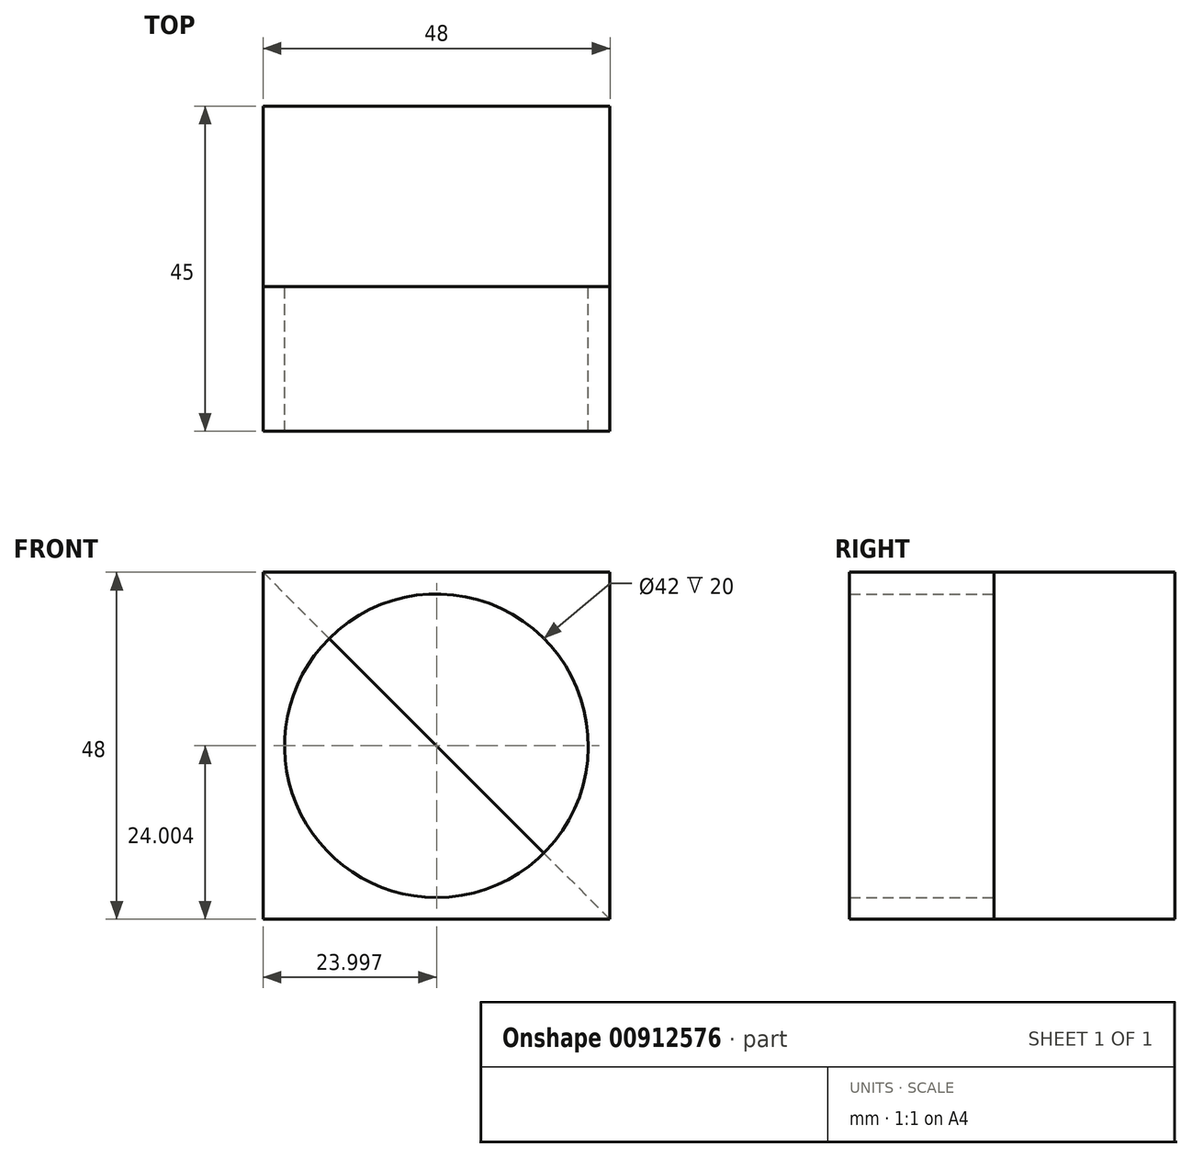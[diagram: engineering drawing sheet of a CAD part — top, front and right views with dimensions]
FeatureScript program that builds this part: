
annotation { "Feature Type Name" : "Feature", "Feature Type Description" : "" }
export const myFeature = defineFeature(function(context is Context, id is Id, definition is map)
    precondition{}
    {
        {
            var Q0;
            Q0=qCreatedBy(makeId("Front.planeOp"),FACE);
            var sketch = newSketch(context, id + "F0", { "sketchPlane" : qUnion([Q0])});
            skLineSegment(sketch, "E0.bottom", {"start": v(-37.2, 26.25) * mm, "end": v(10.8, 26.25) * mm});
            skLineSegment(sketch, "E0.top", {"start": v(-37.2, -21.75) * mm, "end": v(10.8, -21.75) * mm});
            skLineSegment(sketch, "E0.left", {"start": v(-37.2, 26.25) * mm, "end": v(-37.2, -21.75) * mm});
            skLineSegment(sketch, "E0.right", {"start": v(10.8, 26.25) * mm, "end": v(10.8, -21.75) * mm});
            skLineSegment(sketch, "E1", {"start": v(-37.2, 26.25) * mm, "end": v(10.8, -21.75) * mm});
            skLineSegment(sketch, "E2", {"start": v(10.8, 26.25) * mm, "end": v(-37.2, -21.75) * mm});
            skSolve(sketch);
        }
        {
            var Q0;
            {var subQ0=sQuery(id+"F0.wireOp",EDGE,"E0.left");Q0=makeQuery(id+"F0.imprint","IMPRINT",FACE,{"disambiguationData":[TD([[makeQuery(id+"F0.imprint","IMPRINT",EDGE,{"derivedFrom":subQ0}),1.0]])]});}
            var Q1;
            {var subQ0=sQuery(id+"F0.wireOp",EDGE,"E0.bottom");Q1=makeQuery(id+"F0.imprint","IMPRINT",FACE,{"disambiguationData":[TD([[makeQuery(id+"F0.imprint","IMPRINT",EDGE,{"derivedFrom":subQ0}),-1.0]])]});}
            var Q2;
            {var subQ0=sQuery(id+"F0.wireOp",EDGE,"E0.right");Q2=makeQuery(id+"F0.imprint","IMPRINT",FACE,{"disambiguationData":[TD([[makeQuery(id+"F0.imprint","IMPRINT",EDGE,{"derivedFrom":subQ0}),-1.0]])]});}
            var Q3;
            {var subQ0=sQuery(id+"F0.wireOp",EDGE,"E0.top");Q3=makeQuery(id+"F0.imprint","IMPRINT",FACE,{"disambiguationData":[TD([[makeQuery(id+"F0.imprint","IMPRINT",EDGE,{"derivedFrom":subQ0}),1.0]])]});}
            extrude(context, id + "F1", {"entities" : qUnion([Q0, Q1, Q2, Q3]), "depth" : 20 * mm, "offsetDistance" : 25 * mm});
        }
        {
            var Q0;
            Q0=makeQuery(id+"F1.opExtrude","CAP_FACE",FACE,{"disambiguationData":[OSD([sQuery(id+"F0.wireOp",EDGE,"E0.bottom"),sQuery(id+"F0.wireOp",EDGE,"E0.top"),sQuery(id+"F0.wireOp",EDGE,"E0.left"),sQuery(id+"F0.wireOp",EDGE,"E0.right")])],"isStart":true});
            var sketch = newSketch(context, id + "F2", { "sketchPlane" : qUnion([Q0])});
            skLineSegment(sketch, "E3", {"start": v(37.2, -21.75) * mm, "end": v(-10.8, 26.25) * mm});
            skLineSegment(sketch, "E4", {"start": v(-10.8, 26.25) * mm, "end": v(-10.8, -21.75) * mm});
            skLineSegment(sketch, "E5", {"start": v(-10.8, -21.75) * mm, "end": v(37.2, 26.25) * mm});
            skLineSegment(sketch, "E6", {"start": v(37.2, 26.25) * mm, "end": v(13.2, 2.25) * mm});
            skLineSegment(sketch, "E7", {"start": v(13.2, 2.25) * mm, "end": v(13.2, 26.25) * mm});
            skLineSegment(sketch, "E8", {"start": v(13.2, 26.25) * mm, "end": v(13.2, 2.25) * mm});
            skSolve(sketch);
        }
        {
            var Q0;
            Q0=sQuery(id+"F2.wireOp",VERTEX,"E6.end");
            var Q1;
            Q1=makeQuery(id+"F1.opExtrude","SWEPT_BODY",BODY,{"disambiguationData":[OSD([sQuery(id+"F0.wireOp",EDGE,"E0.bottom"),sQuery(id+"F0.wireOp",EDGE,"E0.top"),sQuery(id+"F0.wireOp",EDGE,"E0.left"),sQuery(id+"F0.wireOp",EDGE,"E0.right")])]});
            hole(context, id + "F3", {"style" : HoleStyle.SIMPLE, "endStyle" : HoleEndStyle.BLIND, "holeDiameter" : 42 * mm, "majorDiameter" : 5 * mm, "holeDepth" : 50 * mm, "isTappedThrough" : true, "tappedDepth" : 12 * mm, "tapClearance" : 3, "locations" : qUnion([Q0]), "scope" : qUnion([Q1])});
        }
        {
            var Q0;
            {var subQ2=sQuery(id+"F2.wireOp",EDGE,"E5");Q0=makeQuery(id+"F2.imprint","IMPRINT",FACE,{"disambiguationData":[TD([[makeQuery(id+"F2.imprint","IMPRINT",EDGE,{"derivedFrom":subQ2}),-1.0]])]});}
            var Q1;
            {var subQ0=sQuery(id+"F2.wireOp",EDGE,"E6");Q1=makeQuery(id+"F2.imprint","IMPRINT",FACE,{"disambiguationData":[TD([[makeQuery(id+"F2.imprint","IMPRINT",EDGE,{"derivedFrom":subQ0}),-1.0]])]});}
            var Q2;
            {var subQ2=sQuery(id+"F2.wireOp",EDGE,"E6");Q2=makeQuery(id+"F2.imprint","IMPRINT",FACE,{"disambiguationData":[TD([[makeQuery(id+"F2.imprint","IMPRINT",EDGE,{"derivedFrom":subQ2}),1.0]])]});}
            extrude(context, id + "F4", {"entities" : qUnion([Q0, Q1, Q2]), "operationType" : NewBodyOperationType.ADD, "depth" : 25 * mm, "offsetDistance" : 25 * mm});
        }
    });
